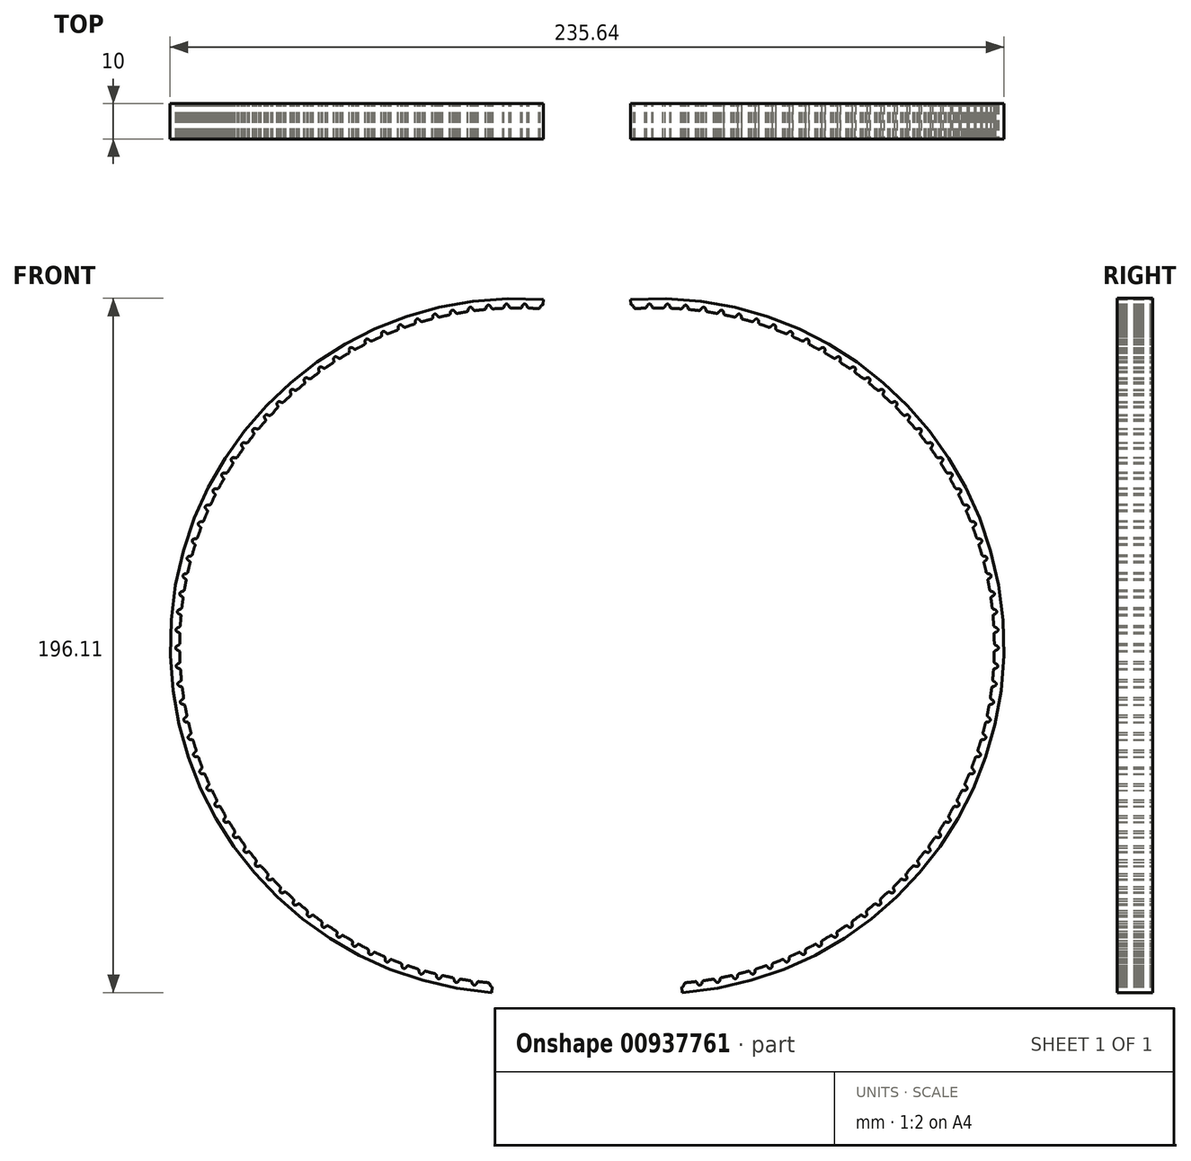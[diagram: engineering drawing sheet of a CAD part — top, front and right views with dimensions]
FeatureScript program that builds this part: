
annotation { "Feature Type Name" : "Feature", "Feature Type Description" : "" }
export const myFeature = defineFeature(function(context is Context, id is Id, definition is map)
    precondition{}
    {
        {
            var Q0;
            Q0=qCreatedBy(makeId("Front.planeOp"),FACE);
            var sketch = newSketch(context, id + "F0", { "sketchPlane" : qUnion([Q0])});
            skArc(sketch, "E0", {"start": v(26.92, -113.75) * mm, "mid": v(117.55, -8.54) * mm, "end": v(12.34, 82.09) * mm});
            skEllipticalArc(sketch, "E1.5.0.0", {});
            skArc(sketch, "E1.5.0.1", {"start": v(13.25, 79.82) * mm, "mid": v(13.37, 79.62) * mm, "end": v(13.55, 79.46) * mm});
            skEllipticalArc(sketch, "E1.5.0.3", {});
            skArc(sketch, "E2.1.0", {"start": v(16.42, 79.6) * mm, "mid": v(16.72, 79.76) * mm, "end": v(16.92, 80.04) * mm});
            skEllipticalArc(sketch, "E2.1.1", {});
            skArc(sketch, "E2.2.0", {"start": v(21.5, 79.64) * mm, "mid": v(21.81, 79.78) * mm, "end": v(22.03, 80.05) * mm});
            skEllipticalArc(sketch, "E2.2.1", {});
            skArc(sketch, "E2.3.0", {"start": v(26.58, 79.4) * mm, "mid": v(26.9, 79.53) * mm, "end": v(27.13, 79.79) * mm});
            skEllipticalArc(sketch, "E2.3.1", {});
            skArc(sketch, "E2.4.0", {"start": v(31.64, 78.9) * mm, "mid": v(31.96, 79) * mm, "end": v(32.2, 79.25) * mm});
            skEllipticalArc(sketch, "E2.4.1", {});
            skArc(sketch, "E2.5.0", {"start": v(36.67, 78.12) * mm, "mid": v(37, 78.22) * mm, "end": v(37.25, 78.45) * mm});
            skEllipticalArc(sketch, "E2.5.1", {});
            skArc(sketch, "E2.6.0", {"start": v(41.64, 77.08) * mm, "mid": v(41.98, 77.16) * mm, "end": v(42.24, 77.38) * mm});
            skEllipticalArc(sketch, "E2.6.1", {});
            skArc(sketch, "E2.7.0", {"start": v(46.56, 75.78) * mm, "mid": v(46.9, 75.84) * mm, "end": v(47.17, 76.04) * mm});
            skEllipticalArc(sketch, "E2.7.1", {});
            skArc(sketch, "E2.8.0", {"start": v(51.4, 74.22) * mm, "mid": v(51.73, 74.26) * mm, "end": v(52.02, 74.44) * mm});
            skEllipticalArc(sketch, "E2.8.1", {});
            skArc(sketch, "E2.9.0", {"start": v(56.14, 72.4) * mm, "mid": v(56.48, 72.42) * mm, "end": v(56.78, 72.6) * mm});
            skEllipticalArc(sketch, "E2.9.1", {});
            skArc(sketch, "E2.10.0", {"start": v(60.79, 70.33) * mm, "mid": v(61.13, 70.34) * mm, "end": v(61.43, 70.49) * mm});
            skEllipticalArc(sketch, "E2.10.1", {});
            skArc(sketch, "E2.11.0", {"start": v(65.31, 68.02) * mm, "mid": v(65.66, 68) * mm, "end": v(65.97, 68.14) * mm});
            skEllipticalArc(sketch, "E2.11.1", {});
            skArc(sketch, "E2.12.0", {"start": v(69.71, 65.47) * mm, "mid": v(70.05, 65.44) * mm, "end": v(70.37, 65.56) * mm});
            skEllipticalArc(sketch, "E2.12.1", {});
            skArc(sketch, "E2.13.0", {"start": v(73.97, 62.69) * mm, "mid": v(74.3, 62.64) * mm, "end": v(74.63, 62.74) * mm});
            skEllipticalArc(sketch, "E2.13.1", {});
            skArc(sketch, "E2.14.0", {"start": v(78.07, 59.69) * mm, "mid": v(78.4, 59.62) * mm, "end": v(78.74, 59.7) * mm});
            skEllipticalArc(sketch, "E2.14.1", {});
            skArc(sketch, "E2.15.0", {"start": v(82, 56.47) * mm, "mid": v(82.34, 56.38) * mm, "end": v(82.67, 56.45) * mm});
            skEllipticalArc(sketch, "E2.15.1", {});
            skArc(sketch, "E2.16.0", {"start": v(85.77, 53.05) * mm, "mid": v(86.1, 52.94) * mm, "end": v(86.43, 53) * mm});
            skEllipticalArc(sketch, "E2.16.1", {});
            skArc(sketch, "E2.17.0", {"start": v(89.34, 49.43) * mm, "mid": v(89.66, 49.3) * mm, "end": v(90, 49.34) * mm});
            skEllipticalArc(sketch, "E2.17.1", {});
            skArc(sketch, "E2.18.0", {"start": v(92.71, 45.63) * mm, "mid": v(93.03, 45.49) * mm, "end": v(93.37, 45.5) * mm});
            skEllipticalArc(sketch, "E2.18.1", {});
            skArc(sketch, "E2.19.0", {"start": v(95.88, 41.65) * mm, "mid": v(96.19, 41.5) * mm, "end": v(96.53, 41.5) * mm});
            skEllipticalArc(sketch, "E2.19.1", {});
            skArc(sketch, "E2.20.0", {"start": v(98.83, 37.5) * mm, "mid": v(99.13, 37.34) * mm, "end": v(99.47, 37.32) * mm});
            skEllipticalArc(sketch, "E2.20.1", {});
            skArc(sketch, "E2.21.0", {"start": v(101.56, 33.22) * mm, "mid": v(101.84, 33.03) * mm, "end": v(102.18, 33) * mm});
            skEllipticalArc(sketch, "E2.21.1", {});
            skArc(sketch, "E2.22.0", {"start": v(104.05, 28.79) * mm, "mid": v(104.33, 28.59) * mm, "end": v(104.67, 28.53) * mm});
            skEllipticalArc(sketch, "E2.22.1", {});
            skArc(sketch, "E2.23.0", {"start": v(106.3, 24.23) * mm, "mid": v(106.57, 24.02) * mm, "end": v(106.9, 23.94) * mm});
            skEllipticalArc(sketch, "E2.23.1", {});
            skArc(sketch, "E2.24.0", {"start": v(108.32, 19.56) * mm, "mid": v(108.57, 19.33) * mm, "end": v(108.9, 19.24) * mm});
            skEllipticalArc(sketch, "E2.24.1", {});
            skArc(sketch, "E2.25.0", {"start": v(110.08, 14.8) * mm, "mid": v(110.32, 14.55) * mm, "end": v(110.64, 14.44) * mm});
            skEllipticalArc(sketch, "E2.25.1", {});
            skArc(sketch, "E2.26.0", {"start": v(111.58, 9.93) * mm, "mid": v(111.8, 9.68) * mm, "end": v(112.12, 9.55) * mm});
            skEllipticalArc(sketch, "E2.26.1", {});
            skArc(sketch, "E2.27.0", {"start": v(112.82, 5) * mm, "mid": v(113.03, 4.74) * mm, "end": v(113.34, 4.6) * mm});
            skEllipticalArc(sketch, "E2.27.1", {});
            skArc(sketch, "E2.28.0", {"start": v(113.8, 0.02) * mm, "mid": v(114, -0.26) * mm, "end": v(114.3, -0.42) * mm});
            skEllipticalArc(sketch, "E2.28.1", {});
            skArc(sketch, "E2.29.0", {"start": v(114.5, -5.02) * mm, "mid": v(114.69, -5.3) * mm, "end": v(114.98, -5.48) * mm});
            skEllipticalArc(sketch, "E2.29.1", {});
            skArc(sketch, "E2.30.0", {"start": v(114.95, -10.08) * mm, "mid": v(115.12, -10.38) * mm, "end": v(115.4, -10.57) * mm});
            skEllipticalArc(sketch, "E2.30.1", {});
            skArc(sketch, "E2.31.0", {"start": v(115.12, -15.16) * mm, "mid": v(115.27, -15.47) * mm, "end": v(115.54, -15.68) * mm});
            skEllipticalArc(sketch, "E2.31.1", {});
            skArc(sketch, "E2.32.0", {"start": v(115.02, -20.25) * mm, "mid": v(115.15, -20.56) * mm, "end": v(115.41, -20.78) * mm});
            skEllipticalArc(sketch, "E2.32.1", {});
            skArc(sketch, "E2.33.0", {"start": v(114.65, -25.32) * mm, "mid": v(114.77, -25.64) * mm, "end": v(115.02, -25.87) * mm});
            skEllipticalArc(sketch, "E2.33.1", {});
            skArc(sketch, "E2.34.0", {"start": v(114, -30.36) * mm, "mid": v(114.1, -30.69) * mm, "end": v(114.35, -30.94) * mm});
            skEllipticalArc(sketch, "E2.34.1", {});
            skArc(sketch, "E2.35.0", {"start": v(113.1, -35.36) * mm, "mid": v(113.19, -35.7) * mm, "end": v(113.4, -35.96) * mm});
            skEllipticalArc(sketch, "E2.35.1", {});
            skArc(sketch, "E2.36.0", {"start": v(111.93, -40.31) * mm, "mid": v(112, -40.65) * mm, "end": v(112.2, -40.92) * mm});
            skEllipticalArc(sketch, "E2.36.1", {});
            skArc(sketch, "E2.37.0", {"start": v(110.5, -45.19) * mm, "mid": v(110.54, -45.53) * mm, "end": v(110.74, -45.8) * mm});
            skEllipticalArc(sketch, "E2.37.1", {});
            skArc(sketch, "E2.38.0", {"start": v(108.8, -49.98) * mm, "mid": v(108.83, -50.32) * mm, "end": v(109.01, -50.62) * mm});
            skEllipticalArc(sketch, "E2.38.1", {});
            skArc(sketch, "E2.39.0", {"start": v(106.86, -54.68) * mm, "mid": v(106.87, -55.02) * mm, "end": v(107.04, -55.32) * mm});
            skEllipticalArc(sketch, "E2.39.1", {});
            skArc(sketch, "E2.40.0", {"start": v(104.67, -59.27) * mm, "mid": v(104.66, -59.61) * mm, "end": v(104.8, -59.92) * mm});
            skEllipticalArc(sketch, "E2.40.1", {});
            skArc(sketch, "E2.41.0", {"start": v(102.24, -63.73) * mm, "mid": v(102.21, -64.07) * mm, "end": v(102.34, -64.4) * mm});
            skEllipticalArc(sketch, "E2.41.1", {});
            skArc(sketch, "E2.42.0", {"start": v(99.57, -68.06) * mm, "mid": v(99.53, -68.4) * mm, "end": v(99.64, -68.72) * mm});
            skEllipticalArc(sketch, "E2.42.1", {});
            skArc(sketch, "E2.43.0", {"start": v(96.68, -72.24) * mm, "mid": v(96.62, -72.58) * mm, "end": v(96.71, -72.9) * mm});
            skEllipticalArc(sketch, "E2.43.1", {});
            skArc(sketch, "E2.44.0", {"start": v(93.57, -76.26) * mm, "mid": v(93.49, -76.6) * mm, "end": v(93.57, -76.93) * mm});
            skEllipticalArc(sketch, "E2.44.1", {});
            skArc(sketch, "E2.45.0", {"start": v(90.25, -80.11) * mm, "mid": v(90.15, -80.44) * mm, "end": v(90.2, -80.78) * mm});
            skEllipticalArc(sketch, "E2.45.1", {});
            skArc(sketch, "E2.46.0", {"start": v(86.72, -83.78) * mm, "mid": v(86.61, -84.1) * mm, "end": v(86.65, -84.44) * mm});
            skEllipticalArc(sketch, "E2.46.1", {});
            skArc(sketch, "E2.47.0", {"start": v(83.01, -87.25) * mm, "mid": v(82.88, -87.57) * mm, "end": v(82.9, -87.91) * mm});
            skEllipticalArc(sketch, "E2.47.1", {});
            skArc(sketch, "E2.48.0", {"start": v(79.12, -90.53) * mm, "mid": v(78.98, -90.84) * mm, "end": v(78.98, -91.18) * mm});
            skEllipticalArc(sketch, "E2.48.1", {});
            skArc(sketch, "E2.49.0", {"start": v(75.06, -93.59) * mm, "mid": v(74.9, -93.89) * mm, "end": v(74.89, -94.23) * mm});
            skEllipticalArc(sketch, "E2.49.1", {});
            skArc(sketch, "E2.50.0", {"start": v(70.85, -96.43) * mm, "mid": v(70.67, -96.72) * mm, "end": v(70.64, -97.06) * mm});
            skEllipticalArc(sketch, "E2.50.1", {});
            skArc(sketch, "E2.51.0", {"start": v(66.48, -99.04) * mm, "mid": v(66.29, -99.32) * mm, "end": v(66.24, -99.66) * mm});
            skEllipticalArc(sketch, "E2.51.1", {});
            skArc(sketch, "E2.52.0", {"start": v(61.99, -101.41) * mm, "mid": v(61.78, -101.68) * mm, "end": v(61.71, -102.02) * mm});
            skEllipticalArc(sketch, "E2.52.1", {});
            skArc(sketch, "E2.53.0", {"start": v(57.37, -103.55) * mm, "mid": v(57.15, -103.8) * mm, "end": v(57.07, -104.14) * mm});
            skEllipticalArc(sketch, "E2.53.1", {});
            skArc(sketch, "E2.54.0", {"start": v(52.65, -105.43) * mm, "mid": v(52.42, -105.68) * mm, "end": v(52.31, -106) * mm});
            skEllipticalArc(sketch, "E2.54.1", {});
            skArc(sketch, "E2.55.0", {"start": v(47.84, -107.06) * mm, "mid": v(47.59, -107.3) * mm, "end": v(47.47, -107.62) * mm});
            skEllipticalArc(sketch, "E2.55.1", {});
            skArc(sketch, "E2.56.0", {"start": v(42.94, -108.43) * mm, "mid": v(42.68, -108.65) * mm, "end": v(42.54, -108.97) * mm});
            skEllipticalArc(sketch, "E2.56.1", {});
            skArc(sketch, "E2.57.0", {"start": v(37.98, -109.54) * mm, "mid": v(37.7, -109.75) * mm, "end": v(37.55, -110.06) * mm});
            skEllipticalArc(sketch, "E2.57.1", {});
            skArc(sketch, "E2.58.0", {"start": v(32.97, -110.39) * mm, "mid": v(32.68, -110.58) * mm, "end": v(32.51, -110.88) * mm});
            skEllipticalArc(sketch, "E2.58.1", {});
            skArc(sketch, "E2.59.0", {"start": v(27.92, -110.96) * mm, "mid": v(27.62, -111.14) * mm, "end": v(27.44, -111.43) * mm});
            skEllipticalArc(sketch, "E2.59.1", {});
            skLineSegment(sketch, "E2.anchor1", {"start": v(19.63, -15.83) * mm, "end": v(11.34, 79.3) * mm, "construction": true});
            skLineSegment(sketch, "E2.anchor2", {"start": v(19.63, -15.83) * mm, "end": v(27.92, -110.96) * mm, "construction": true});
            skArc(sketch, "E3.1.0", {"start": v(18.35, 80.02) * mm, "mid": v(18.46, 79.81) * mm, "end": v(18.63, 79.65) * mm});
            skArc(sketch, "E3.2.0", {"start": v(23.45, 79.96) * mm, "mid": v(23.55, 79.74) * mm, "end": v(23.7, 79.57) * mm});
            skArc(sketch, "E3.3.0", {"start": v(28.54, 79.62) * mm, "mid": v(28.63, 79.4) * mm, "end": v(28.78, 79.22) * mm});
            skArc(sketch, "E3.4.0", {"start": v(33.61, 79) * mm, "mid": v(33.69, 78.78) * mm, "end": v(33.83, 78.6) * mm});
            skArc(sketch, "E3.5.0", {"start": v(38.64, 78.13) * mm, "mid": v(38.7, 77.9) * mm, "end": v(38.83, 77.7) * mm});
            skArc(sketch, "E3.6.0", {"start": v(43.61, 76.98) * mm, "mid": v(43.66, 76.75) * mm, "end": v(43.78, 76.55) * mm});
            skArc(sketch, "E3.7.0", {"start": v(48.52, 75.58) * mm, "mid": v(48.56, 75.34) * mm, "end": v(48.67, 75.13) * mm});
            skArc(sketch, "E3.8.0", {"start": v(53.34, 73.9) * mm, "mid": v(53.37, 73.67) * mm, "end": v(53.47, 73.46) * mm});
            skArc(sketch, "E3.9.0", {"start": v(58.07, 71.99) * mm, "mid": v(58.08, 71.75) * mm, "end": v(58.17, 71.53) * mm});
            skArc(sketch, "E3.10.0", {"start": v(62.69, 69.82) * mm, "mid": v(62.7, 69.58) * mm, "end": v(62.77, 69.36) * mm});
            skArc(sketch, "E3.11.0", {"start": v(67.19, 67.4) * mm, "mid": v(67.18, 67.17) * mm, "end": v(67.24, 66.94) * mm});
            skArc(sketch, "E3.12.0", {"start": v(71.55, 64.75) * mm, "mid": v(71.53, 64.52) * mm, "end": v(71.58, 64.3) * mm});
            skArc(sketch, "E3.13.0", {"start": v(75.77, 61.88) * mm, "mid": v(75.73, 61.64) * mm, "end": v(75.77, 61.41) * mm});
            skArc(sketch, "E3.14.0", {"start": v(79.82, 58.78) * mm, "mid": v(79.77, 58.55) * mm, "end": v(79.8, 58.31) * mm});
            skArc(sketch, "E3.15.0", {"start": v(83.7, 55.47) * mm, "mid": v(83.65, 55.24) * mm, "end": v(83.66, 55) * mm});
            skArc(sketch, "E3.16.0", {"start": v(87.41, 51.96) * mm, "mid": v(87.34, 51.73) * mm, "end": v(87.34, 51.5) * mm});
            skArc(sketch, "E3.17.0", {"start": v(90.92, 48.25) * mm, "mid": v(90.83, 47.95) * mm, "end": v(90.86, 47.64) * mm});
            skArc(sketch, "E3.18.0", {"start": v(94.23, 44.37) * mm, "mid": v(94.12, 44.08) * mm, "end": v(94.14, 43.76) * mm});
            skArc(sketch, "E3.19.0", {"start": v(97.33, 40.31) * mm, "mid": v(97.2, 40.03) * mm, "end": v(97.2, 39.71) * mm});
            skArc(sketch, "E3.20.0", {"start": v(100.21, 36.1) * mm, "mid": v(100.07, 35.82) * mm, "end": v(100.05, 35.5) * mm});
            skArc(sketch, "E3.21.0", {"start": v(102.86, 31.74) * mm, "mid": v(102.7, 31.46) * mm, "end": v(102.67, 31.15) * mm});
            skArc(sketch, "E3.22.0", {"start": v(105.27, 27.24) * mm, "mid": v(105.1, 26.98) * mm, "end": v(105.05, 26.66) * mm});
            skArc(sketch, "E3.23.0", {"start": v(107.44, 22.62) * mm, "mid": v(107.26, 22.37) * mm, "end": v(107.2, 22.06) * mm});
            skArc(sketch, "E3.24.0", {"start": v(109.37, 17.9) * mm, "mid": v(109.17, 17.65) * mm, "end": v(109.09, 17.34) * mm});
            skArc(sketch, "E3.25.0", {"start": v(111.03, 13.07) * mm, "mid": v(110.82, 12.83) * mm, "end": v(110.73, 12.54) * mm});
            skArc(sketch, "E3.26.0", {"start": v(112.44, 8.16) * mm, "mid": v(112.22, 7.94) * mm, "end": v(112.1, 7.65) * mm});
            skArc(sketch, "E3.27.0", {"start": v(113.59, 3.19) * mm, "mid": v(113.35, 2.98) * mm, "end": v(113.23, 2.7) * mm});
            skArc(sketch, "E3.28.0", {"start": v(114.47, -1.84) * mm, "mid": v(114.22, -2.04) * mm, "end": v(114.08, -2.32) * mm});
            skArc(sketch, "E3.29.0", {"start": v(115.08, -6.9) * mm, "mid": v(114.82, -7.09) * mm, "end": v(114.66, -7.36) * mm});
            skArc(sketch, "E3.30.0", {"start": v(115.42, -12) * mm, "mid": v(115.15, -12.17) * mm, "end": v(114.98, -12.43) * mm});
            skArc(sketch, "E3.31.0", {"start": v(115.49, -17.1) * mm, "mid": v(115.21, -17.26) * mm, "end": v(115.03, -17.51) * mm});
            skArc(sketch, "E3.32.0", {"start": v(115.28, -22.2) * mm, "mid": v(115, -22.34) * mm, "end": v(114.8, -22.59) * mm});
            skArc(sketch, "E3.33.0", {"start": v(114.8, -27.28) * mm, "mid": v(114.52, -27.4) * mm, "end": v(114.3, -27.64) * mm});
            skArc(sketch, "E3.34.0", {"start": v(114.06, -32.33) * mm, "mid": v(113.77, -32.44) * mm, "end": v(113.54, -32.66) * mm});
            skArc(sketch, "E3.35.0", {"start": v(113.05, -37.34) * mm, "mid": v(112.75, -37.43) * mm, "end": v(112.52, -37.64) * mm});
            skArc(sketch, "E3.36.0", {"start": v(111.78, -42.28) * mm, "mid": v(111.47, -42.36) * mm, "end": v(111.22, -42.55) * mm});
            skArc(sketch, "E3.37.0", {"start": v(110.24, -47.14) * mm, "mid": v(109.93, -47.2) * mm, "end": v(109.67, -47.39) * mm});
            skArc(sketch, "E3.38.0", {"start": v(108.44, -51.92) * mm, "mid": v(108.13, -51.97) * mm, "end": v(107.86, -52.14) * mm});
            skArc(sketch, "E3.39.0", {"start": v(106.4, -56.6) * mm, "mid": v(106.08, -56.63) * mm, "end": v(105.8, -56.78) * mm});
            skArc(sketch, "E3.40.0", {"start": v(104.1, -61.16) * mm, "mid": v(103.79, -61.17) * mm, "end": v(103.5, -61.3) * mm});
            skArc(sketch, "E3.41.0", {"start": v(101.57, -65.59) * mm, "mid": v(101.26, -65.58) * mm, "end": v(100.97, -65.7) * mm});
            skArc(sketch, "E3.42.0", {"start": v(98.8, -69.88) * mm, "mid": v(98.5, -69.86) * mm, "end": v(98.2, -69.97) * mm});
            skArc(sketch, "E3.43.0", {"start": v(95.82, -74.02) * mm, "mid": v(95.5, -73.98) * mm, "end": v(95.2, -74.07) * mm});
            skArc(sketch, "E3.44.0", {"start": v(92.61, -77.99) * mm, "mid": v(92.3, -77.93) * mm, "end": v(92, -78.01) * mm});
            skArc(sketch, "E3.45.0", {"start": v(89.2, -81.79) * mm, "mid": v(88.9, -81.71) * mm, "end": v(88.59, -81.77) * mm});
            skArc(sketch, "E3.46.0", {"start": v(85.6, -85.4) * mm, "mid": v(85.3, -85.3) * mm, "end": v(84.98, -85.35) * mm});
            skArc(sketch, "E3.47.0", {"start": v(81.8, -88.8) * mm, "mid": v(81.5, -88.7) * mm, "end": v(81.19, -88.73) * mm});
            skArc(sketch, "E3.48.0", {"start": v(77.83, -92.01) * mm, "mid": v(77.53, -91.9) * mm, "end": v(77.22, -91.9) * mm});
            skArc(sketch, "E3.49.0", {"start": v(73.69, -95) * mm, "mid": v(73.4, -94.87) * mm, "end": v(73.09, -94.86) * mm});
            skArc(sketch, "E3.50.0", {"start": v(69.4, -97.77) * mm, "mid": v(69.12, -97.62) * mm, "end": v(68.8, -97.6) * mm});
            skArc(sketch, "E3.51.0", {"start": v(64.97, -100.3) * mm, "mid": v(64.7, -100.14) * mm, "end": v(64.39, -100.1) * mm});
            skArc(sketch, "E3.52.0", {"start": v(60.4, -102.6) * mm, "mid": v(60.15, -102.41) * mm, "end": v(59.84, -102.36) * mm});
            skArc(sketch, "E3.53.0", {"start": v(55.73, -104.64) * mm, "mid": v(55.48, -104.45) * mm, "end": v(55.18, -104.38) * mm});
            skArc(sketch, "E3.54.0", {"start": v(50.95, -106.44) * mm, "mid": v(50.72, -106.23) * mm, "end": v(50.41, -106.14) * mm});
            skArc(sketch, "E3.55.0", {"start": v(46.09, -107.97) * mm, "mid": v(45.86, -107.76) * mm, "end": v(45.56, -107.65) * mm});
            skArc(sketch, "E3.56.0", {"start": v(41.15, -109.25) * mm, "mid": v(40.93, -109.02) * mm, "end": v(40.64, -108.9) * mm});
            skArc(sketch, "E3.57.0", {"start": v(36.14, -110.27) * mm, "mid": v(35.94, -110.02) * mm, "end": v(35.66, -109.89) * mm});
            skArc(sketch, "E3.58.0", {"start": v(31.1, -111.01) * mm, "mid": v(30.9, -110.76) * mm, "end": v(30.63, -110.6) * mm});
            skLineSegment(sketch, "E3.anchor1", {"start": v(19.63, -15.83) * mm, "end": v(13.25, 79.82) * mm, "construction": true});
            skEllipticalArc(sketch, "E4.1.0", {});
            skEllipticalArc(sketch, "E4.2.0", {});
            skEllipticalArc(sketch, "E4.3.0", {});
            skEllipticalArc(sketch, "E4.4.0", {});
            skEllipticalArc(sketch, "E4.5.0", {});
            skEllipticalArc(sketch, "E4.6.0", {});
            skEllipticalArc(sketch, "E4.7.0", {});
            skEllipticalArc(sketch, "E4.8.0", {});
            skEllipticalArc(sketch, "E4.9.0", {});
            skEllipticalArc(sketch, "E4.10.0", {});
            skEllipticalArc(sketch, "E4.11.0", {});
            skEllipticalArc(sketch, "E4.12.0", {});
            skEllipticalArc(sketch, "E4.13.0", {});
            skEllipticalArc(sketch, "E4.14.0", {});
            skEllipticalArc(sketch, "E4.15.0", {});
            skEllipticalArc(sketch, "E4.16.0", {});
            skEllipticalArc(sketch, "E4.17.0", {});
            skEllipticalArc(sketch, "E4.18.0", {});
            skEllipticalArc(sketch, "E4.19.0", {});
            skEllipticalArc(sketch, "E4.20.0", {});
            skEllipticalArc(sketch, "E4.21.0", {});
            skEllipticalArc(sketch, "E4.22.0", {});
            skEllipticalArc(sketch, "E4.23.0", {});
            skEllipticalArc(sketch, "E4.24.0", {});
            skEllipticalArc(sketch, "E4.25.0", {});
            skEllipticalArc(sketch, "E4.26.0", {});
            skEllipticalArc(sketch, "E4.27.0", {});
            skEllipticalArc(sketch, "E4.28.0", {});
            skEllipticalArc(sketch, "E4.29.0", {});
            skEllipticalArc(sketch, "E4.30.0", {});
            skEllipticalArc(sketch, "E4.31.0", {});
            skEllipticalArc(sketch, "E4.32.0", {});
            skEllipticalArc(sketch, "E4.33.0", {});
            skEllipticalArc(sketch, "E4.34.0", {});
            skEllipticalArc(sketch, "E4.35.0", {});
            skEllipticalArc(sketch, "E4.36.0", {});
            skEllipticalArc(sketch, "E4.37.0", {});
            skEllipticalArc(sketch, "E4.38.0", {});
            skEllipticalArc(sketch, "E4.39.0", {});
            skEllipticalArc(sketch, "E4.40.0", {});
            skEllipticalArc(sketch, "E4.41.0", {});
            skEllipticalArc(sketch, "E4.42.0", {});
            skEllipticalArc(sketch, "E4.43.0", {});
            skEllipticalArc(sketch, "E4.44.0", {});
            skEllipticalArc(sketch, "E4.45.0", {});
            skEllipticalArc(sketch, "E4.46.0", {});
            skEllipticalArc(sketch, "E4.47.0", {});
            skEllipticalArc(sketch, "E4.48.0", {});
            skEllipticalArc(sketch, "E4.49.0", {});
            skEllipticalArc(sketch, "E4.50.0", {});
            skEllipticalArc(sketch, "E4.51.0", {});
            skEllipticalArc(sketch, "E4.52.0", {});
            skEllipticalArc(sketch, "E4.53.0", {});
            skEllipticalArc(sketch, "E4.54.0", {});
            skEllipticalArc(sketch, "E4.55.0", {});
            skEllipticalArc(sketch, "E4.56.0", {});
            skEllipticalArc(sketch, "E4.57.0", {});
            skEllipticalArc(sketch, "E4.58.0", {});
            skLineSegment(sketch, "E4.anchor1", {"start": v(19.63, -15.83) * mm, "end": v(12.53, 79.55) * mm, "construction": true});
            skLineSegment(sketch, "E4.anchor2", {"start": v(19.63, -15.83) * mm, "end": v(26.73, -111.21) * mm, "construction": true});
            skLineSegment(sketch, "E5", {"start": v(12.54, 79.4) * mm, "end": v(12.34, 82.09) * mm});
            skArc(sketch, "E6.trimOffspring", {"start": v(27.92, -110.96) * mm, "mid": v(29.35, -110.83) * mm, "end": v(30.78, -110.67) * mm});
            skLineSegment(sketch, "E7", {"start": v(26.77, -112.21) * mm, "end": v(26.92, -113.75) * mm});
            skArc(sketch, "E8.trimOffspring", {"start": v(32.97, -110.39) * mm, "mid": v(34.39, -110.18) * mm, "end": v(35.8, -109.94) * mm});
            skArc(sketch, "E9.trimOffspring", {"start": v(37.98, -109.54) * mm, "mid": v(39.39, -109.26) * mm, "end": v(40.8, -108.95) * mm});
            skArc(sketch, "E10.trimOffspring", {"start": v(42.94, -108.43) * mm, "mid": v(44.33, -108.07) * mm, "end": v(45.72, -107.69) * mm});
            skArc(sketch, "E11.trimOffspring", {"start": v(47.84, -107.06) * mm, "mid": v(49.2, -106.63) * mm, "end": v(50.57, -106.17) * mm});
            skArc(sketch, "E12.trimOffspring", {"start": v(52.65, -105.43) * mm, "mid": v(54, -104.92) * mm, "end": v(55.34, -104.4) * mm});
            skArc(sketch, "E13.trimOffspring", {"start": v(57.37, -103.55) * mm, "mid": v(58.7, -102.97) * mm, "end": v(60, -102.37) * mm});
            skArc(sketch, "E14.trimOffspring", {"start": v(61.99, -101.41) * mm, "mid": v(63.27, -100.77) * mm, "end": v(64.55, -100.1) * mm});
            skArc(sketch, "E15.trimOffspring", {"start": v(66.48, -99.04) * mm, "mid": v(67.73, -98.32) * mm, "end": v(68.97, -97.59) * mm});
            skArc(sketch, "E16.trimOffspring", {"start": v(70.85, -96.43) * mm, "mid": v(72.05, -95.65) * mm, "end": v(73.25, -94.85) * mm});
            skArc(sketch, "E17.trimOffspring", {"start": v(75.06, -93.59) * mm, "mid": v(76.23, -92.74) * mm, "end": v(77.38, -91.88) * mm});
            skArc(sketch, "E18.trimOffspring", {"start": v(79.12, -90.53) * mm, "mid": v(80.24, -89.62) * mm, "end": v(81.35, -88.7) * mm});
            skArc(sketch, "E19.trimOffspring", {"start": v(83.01, -87.25) * mm, "mid": v(84.08, -86.3) * mm, "end": v(85.14, -85.31) * mm});
            skArc(sketch, "E20.trimOffspring", {"start": v(86.72, -83.78) * mm, "mid": v(87.74, -82.76) * mm, "end": v(88.74, -81.73) * mm});
            skArc(sketch, "E21.trimOffspring", {"start": v(90.25, -80.11) * mm, "mid": v(91.2, -79.04) * mm, "end": v(92.15, -77.96) * mm});
            skArc(sketch, "E22.trimOffspring", {"start": v(93.57, -76.26) * mm, "mid": v(94.47, -75.14) * mm, "end": v(95.35, -74) * mm});
            skArc(sketch, "E23.trimOffspring", {"start": v(96.68, -72.24) * mm, "mid": v(97.52, -71.08) * mm, "end": v(98.34, -69.9) * mm});
            skArc(sketch, "E24.trimOffspring", {"start": v(99.57, -68.06) * mm, "mid": v(100.35, -66.85) * mm, "end": v(101.1, -65.63) * mm});
            skArc(sketch, "E25.trimOffspring", {"start": v(102.24, -63.73) * mm, "mid": v(102.95, -62.48) * mm, "end": v(103.64, -61.22) * mm});
            skArc(sketch, "E26.trimOffspring", {"start": v(104.67, -59.27) * mm, "mid": v(105.31, -57.98) * mm, "end": v(105.94, -56.69) * mm});
            skArc(sketch, "E27.trimOffspring", {"start": v(106.86, -54.68) * mm, "mid": v(107.44, -53.36) * mm, "end": v(108, -52.04) * mm});
            skArc(sketch, "E28.trimOffspring", {"start": v(108.8, -49.98) * mm, "mid": v(109.3, -48.64) * mm, "end": v(109.8, -47.28) * mm});
            skArc(sketch, "E29.trimOffspring", {"start": v(110.5, -45.19) * mm, "mid": v(110.93, -43.82) * mm, "end": v(111.34, -42.44) * mm});
            skArc(sketch, "E30.trimOffspring", {"start": v(111.93, -40.31) * mm, "mid": v(112.29, -38.92) * mm, "end": v(112.63, -37.52) * mm});
            skArc(sketch, "E31.trimOffspring", {"start": v(113.1, -35.36) * mm, "mid": v(113.39, -33.95) * mm, "end": v(113.65, -32.54) * mm});
            skArc(sketch, "E32.trimOffspring", {"start": v(114, -30.36) * mm, "mid": v(114.22, -28.94) * mm, "end": v(114.4, -27.51) * mm});
            skArc(sketch, "E33.trimOffspring", {"start": v(114.65, -25.32) * mm, "mid": v(114.78, -23.89) * mm, "end": v(114.9, -22.45) * mm});
            skArc(sketch, "E34.trimOffspring", {"start": v(115.02, -20.25) * mm, "mid": v(115.07, -18.81) * mm, "end": v(115.1, -17.37) * mm});
            skArc(sketch, "E35.trimOffspring", {"start": v(115.12, -15.16) * mm, "mid": v(115.1, -13.73) * mm, "end": v(115.05, -12.29) * mm});
            skArc(sketch, "E36.trimOffspring", {"start": v(114.95, -10.08) * mm, "mid": v(114.85, -8.65) * mm, "end": v(114.73, -7.21) * mm});
            skArc(sketch, "E37.trimOffspring", {"start": v(114.5, -5.02) * mm, "mid": v(114.33, -3.6) * mm, "end": v(114.14, -2.17) * mm});
            skArc(sketch, "E38.trimOffspring", {"start": v(113.8, 0.02) * mm, "mid": v(113.55, 1.43) * mm, "end": v(113.28, 2.85) * mm});
            skArc(sketch, "E39.trimOffspring", {"start": v(112.82, 5) * mm, "mid": v(112.5, 6.4) * mm, "end": v(112.15, 7.8) * mm});
            skArc(sketch, "E40.trimOffspring", {"start": v(111.58, 9.93) * mm, "mid": v(111.18, 11.32) * mm, "end": v(110.76, 12.7) * mm});
            skArc(sketch, "E41.trimOffspring", {"start": v(110.08, 14.8) * mm, "mid": v(109.6, 16.15) * mm, "end": v(109.11, 17.5) * mm});
            skArc(sketch, "E42.trimOffspring", {"start": v(108.32, 19.56) * mm, "mid": v(107.77, 20.9) * mm, "end": v(107.21, 22.22) * mm});
            skArc(sketch, "E43.trimOffspring", {"start": v(106.3, 24.23) * mm, "mid": v(105.7, 25.53) * mm, "end": v(105.06, 26.83) * mm});
            skArc(sketch, "E44.trimOffspring", {"start": v(104.05, 28.79) * mm, "mid": v(103.37, 30.06) * mm, "end": v(102.67, 31.31) * mm});
            skArc(sketch, "E45.trimOffspring", {"start": v(101.56, 33.22) * mm, "mid": v(100.81, 34.45) * mm, "end": v(100.04, 35.66) * mm});
            skArc(sketch, "E46.trimOffspring", {"start": v(98.83, 37.5) * mm, "mid": v(98.02, 38.7) * mm, "end": v(97.19, 39.87) * mm});
            skArc(sketch, "E47.trimOffspring", {"start": v(95.88, 41.65) * mm, "mid": v(95, 42.8) * mm, "end": v(94.11, 43.92) * mm});
            skArc(sketch, "E48.trimOffspring", {"start": v(92.71, 45.63) * mm, "mid": v(91.78, 46.72) * mm, "end": v(90.83, 47.8) * mm});
            skArc(sketch, "E49.trimOffspring", {"start": v(89.34, 49.43) * mm, "mid": v(88.35, 50.47) * mm, "end": v(87.34, 51.5) * mm});
            skArc(sketch, "E50.trimOffspring", {"start": v(85.77, 53.05) * mm, "mid": v(84.72, 54.03) * mm, "end": v(83.66, 55) * mm});
            skPoint(sketch, "E51.orphan", {"position": v(87.38, 51.34) * mm});
            skArc(sketch, "E52.trimOffspring", {"start": v(82, 56.47) * mm, "mid": v(80.91, 57.4) * mm, "end": v(79.8, 58.31) * mm});
            skPoint(sketch, "E53.orphan", {"position": v(83.71, 54.85) * mm});
            skArc(sketch, "E54.trimOffspring", {"start": v(78.07, 59.69) * mm, "mid": v(76.93, 60.56) * mm, "end": v(75.77, 61.41) * mm});
            skPoint(sketch, "E55.orphan", {"position": v(79.86, 58.16) * mm});
            skArc(sketch, "E56.trimOffspring", {"start": v(73.97, 62.69) * mm, "mid": v(72.78, 63.5) * mm, "end": v(71.58, 64.3) * mm});
            skPoint(sketch, "E57.orphan", {"position": v(75.84, 61.26) * mm});
            skArc(sketch, "E58.trimOffspring", {"start": v(69.71, 65.47) * mm, "mid": v(68.48, 66.21) * mm, "end": v(67.24, 66.94) * mm});
            skPoint(sketch, "E59.orphan", {"position": v(71.65, 64.15) * mm});
            skArc(sketch, "E60.trimOffspring", {"start": v(65.31, 68.02) * mm, "mid": v(64.05, 68.7) * mm, "end": v(62.77, 69.36) * mm});
            skPoint(sketch, "E61.orphan", {"position": v(67.32, 66.8) * mm});
            skArc(sketch, "E62.trimOffspring", {"start": v(60.79, 70.33) * mm, "mid": v(59.48, 70.94) * mm, "end": v(58.17, 71.53) * mm});
            skPoint(sketch, "E63.orphan", {"position": v(62.86, 69.22) * mm});
            skArc(sketch, "E64.trimOffspring", {"start": v(56.14, 72.4) * mm, "mid": v(54.8, 72.94) * mm, "end": v(53.47, 73.46) * mm});
            skPoint(sketch, "E65.orphan", {"position": v(58.27, 71.4) * mm});
            skArc(sketch, "E66.trimOffspring", {"start": v(51.4, 74.22) * mm, "mid": v(50.03, 74.69) * mm, "end": v(48.67, 75.13) * mm});
            skPoint(sketch, "E67.orphan", {"position": v(53.57, 73.34) * mm});
            skArc(sketch, "E68.trimOffspring", {"start": v(46.56, 75.78) * mm, "mid": v(45.17, 76.18) * mm, "end": v(43.78, 76.55) * mm});
            skPoint(sketch, "E69.orphan", {"position": v(48.78, 75.02) * mm});
            skArc(sketch, "E70.trimOffspring", {"start": v(41.64, 77.08) * mm, "mid": v(40.24, 77.4) * mm, "end": v(38.83, 77.7) * mm});
            skPoint(sketch, "E71.orphan", {"position": v(43.9, 76.44) * mm});
            skArc(sketch, "E72.trimOffspring", {"start": v(36.67, 78.12) * mm, "mid": v(35.25, 78.37) * mm, "end": v(33.83, 78.6) * mm});
            skPoint(sketch, "E73.orphan", {"position": v(38.95, 77.6) * mm});
            skArc(sketch, "E74.trimOffspring", {"start": v(31.64, 78.9) * mm, "mid": v(30.21, 79.07) * mm, "end": v(28.78, 79.22) * mm});
            skPoint(sketch, "E75.orphan", {"position": v(33.95, 78.5) * mm});
            skArc(sketch, "E76.trimOffspring", {"start": v(26.58, 79.4) * mm, "mid": v(25.15, 79.5) * mm, "end": v(23.7, 79.57) * mm});
            skPoint(sketch, "E77.orphan", {"position": v(28.91, 79.12) * mm});
            skArc(sketch, "E78.trimOffspring", {"start": v(21.5, 79.64) * mm, "mid": v(20.06, 79.66) * mm, "end": v(18.63, 79.65) * mm});
            skPoint(sketch, "E79.orphan", {"position": v(23.85, 79.48) * mm});
            skArc(sketch, "E80.trimOffspring", {"start": v(16.42, 79.6) * mm, "mid": v(14.98, 79.54) * mm, "end": v(13.55, 79.46) * mm});
            skPoint(sketch, "E81.orphan", {"position": v(18.77, 79.57) * mm});
            skPoint(sketch, "E82.orphan", {"position": v(13.7, 79.4) * mm});
            skPoint(sketch, "E83.orphan", {"position": v(11.82, 79.76) * mm});
            const initialGuessF0  = {"E1.5.0.0": [0.012530169083424244, 0.07954509625101978, -0.04082935197852619, 0.9991661343425395, 0.001, 0.0007199110732306023, 6.2831853071795845, 0.046258649843688854], "E1.5.0.3": [0.012530169083423734, 0.07954509625102026, -0.040829351978506234, 0.9991661343425403, 0.001, 0.00075, 4.9589597933309815, 0], "E2.1.1": [0.017616482165393188, 0.0797877933801241, 0.012406310336910385, 0.9999230387703968, 0.001, 0.0007199110732306023, 6.2831853071795845, 1.324225513848637], "E2.2.1": [0.0227085032628806, 0.0797594418893875, 0.06560680561779511, 0.9978455527067449, 0.001, 0.0007199110732306023, 6.2831853071795845, 1.324225513848637], "E2.3.1": [0.027791798488855504, 0.07946012214419074, 0.11862133128020791, 0.9929395650115425, 0.001, 0.0007199110732306023, 6.2831853071795845, 1.324225513848637], "E2.4.1": [0.03285195869071776, 0.07889068259887164, 0.17129961189131737, 0.9852189822399303, 0.001, 0.0007199110732306023, 6.2831853071795845, 1.324225513848637], "E2.5.1": [0.03787464029460662, 0.07805273739168897, 0.2234923251414217, 0.9747056892225884, 0.001, 0.0007199110732306023, 6.2831853071795845, 1.324225513848637], "E2.6.1": [0.04284560596381918, 0.07694866176937233, 0.275051525114259, 0.9614294870308068, 0.001, 0.0007199110732306023, 6.2831853071795845, 1.324225513848637], "E2.7.1": [0.047750764956088196, 0.07558158535422708, 0.32583106165578113, 0.9454280085021105, 0.001, 0.0007199110732306023, 6.2831853071795845, 1.324225513848637], "E2.8.1": [0.05257621306532181, 0.07395538327288, 0.37568699465264327, 0.9267466115658934, 0.001, 0.0007199110732306023, 6.2831853071795845, 1.324225513848637], "E2.9.1": [0.05730827203458649, 0.07207466517181176, 0.42447800204609437, 0.9054382506714392, 0.001, 0.0007199110732306023, 6.2831853071795845, 1.324225513848637], "E2.10.1": [0.061933528328612285, 0.06994476215081326, 0.4720657804247066, 0.8815633266827816, 0.001, 0.0007199110732306022, 6.2831853071795845, 1.324225513848637], "E2.11.1": [0.06643887115591601, 0.06757171165140397, 0.5183154370604216, 0.8551895156658926, 0.001, 0.0007199110732306023, 6.2831853071795845, 1.324225513848637], "E2.12.1": [0.07081152963276406, 0.06496224034304802, 0.5630958722766432, 0.8263915770535216, 0.001, 0.0007199110732306023, 6.2831853071795845, 1.324225513848637], "E2.13.1": [0.07503910898362987, 0.06212374505567886, 0.6062801510645143, 0.7952511417314595, 0.001, 0.0007199110732306023, 6.2831853071795845, 1.324225513848637], "E2.14.1": [0.07910962567553179, 0.059064271812581004, 0.647745862893991, 0.7618564806469255, 0.001, 0.0007199110732306023, 6.2831853071795845, 1.324225513848637], "E2.15.1": [0.08301154138665935, 0.05579249302306301, 0.6873754686997893, 0.7263022545949758, 0.001, 0.0007199110732306023, 6.2831853071795845, 1.324225513848637], "E2.16.1": [0.08673379571299994, 0.052317682899571005, 0.7250566340586357, 0.6886892458921962, 0.001, 0.0007199110732306023, 6.2831853071795845, 1.324225513848637], "E2.17.1": [0.09026583752025577, 0.048649691168925896, 0.7606825476133946, 0.6491240726982753, 0.001, 0.0007199110732306023, 6.2831853071795845, 1.324225513848637], "E2.18.1": [0.09359765485218027, 0.04479891515220258, 0.7941522238414651, 0.6077188867952482, 0.001, 0.0007199110732306023, 6.2831853071795845, 1.324225513848637], "E2.19.1": [0.09671980331055585, 0.0407762702923937, 0.8253707893092164, 0.5645910556810844, 0.001, 0.0007199110732306023, 6.2831853071795845, 1.324225513848637], "E2.20.1": [0.09962343282636688, 0.036593159213400575, 0.8542497516010429, 0.519862829878764, 0.001, 0.0007199110732306023, 6.2831853071795845, 1.324225513848637], "E2.21.1": [0.10230031274628161, 0.032261439398056896, 0.880707250160731, 0.47366099640388765, 0.001, 0.0007199110732306023, 6.2831853071795845, 1.324225513848637], "E2.22.1": [0.10474285516333351, 0.02779338957680533, 0.9046682883340994, 0.4261165193731064, 0.001, 0.0007199110732306023, 6.2831853071795845, 1.324225513848637], "E2.23.1": [0.10694413642566782, 0.0232016749223021, 0.9260649459551632, 0.3773641687721038, 0.001, 0.0007199110732306023, 6.2831853071795845, 1.324225513848637], "E2.24.1": [0.108897916762385, 0.018499311148609, 0.944836571873224, 0.3275421384354296, 0.001, 0.0007199110732306023, 6.2831853071795845, 1.324225513848637], "E2.25.1": [0.11059865797084927, 0.013699627616737806, 0.9609299558751463, 0.2767916543210608, 0.001, 0.0007199110732306023, 6.2831853071795845, 1.324225513848637], "E2.26.1": [0.1120415391153257, 0.00881622955112834, 0.9742994795154868, 0.2252565741900813, 0.001, 0.0007199110732306023, 6.2831853071795845, 1.324225513848637], "E2.27.1": [0.1132224701924463, 0.003862959474161565, 0.9849072454269355, 0.17308297982622728, 0.001, 0.0007199110732306023, 6.2831853071795845, 1.324225513848637], "E2.28.1": [0.11413810372476901, -0.0011461420319740711, 0.9927231847445203, 0.12041876295119949, 0.001, 0.0007199110732306023, 6.2831853071795845, 1.324225513848637], "E2.29.1": [0.11478584424956612, -0.0061968761248381455, 0.9977251423390708, 0.06741320600951253, 0.001, 0.0007199110732306023, 6.2831853071795845, 1.324225513848637], "E2.30.1": [0.1151638556759453, -0.011274925949899992, 0.9998989396183405, 0.014216559011184321, 0.001, 0.0007199110732306023, 6.2831853071795845, 1.324225513848637], "E2.31.1": [0.11527106648944889, -0.016365897223218254, 0.9992384147177656, -0.03902038636824013, 0.001, 0.0007199110732306023, 6.2831853071795845, 1.324225513848637], "E2.32.1": [0.11510717278937796, -0.021455359033602624, 0.9957454399669408, -0.09214672422307635, 0.001, 0.0007199110732306023, 6.2831853071795845, 1.324225513848637], "E2.33.1": [0.11467263915023183, -0.02652888474859949, 0.9894299165822965, -0.14501186217668555, 0.001, 0.0007199110732306023, 6.2831853071795845, 1.324225513848637], "E2.34.1": [0.1139686973048212, -0.031572092908348975, 0.9803097466010259, -0.19746594825192698, 0.001, 0.0007199110732306023, 6.2831853071795845, 1.324225513848637], "E2.35.1": [0.11299734265278771, -0.03657068799139547, 0.9684107821358152, -0.2493602956428686, 0.001, 0.0007199110732306023, 6.2831853071795845, 1.324225513848637], "E2.36.1": [0.11176132860442675, -0.041510500936896386, 0.9537667520942216, -0.3005478041836936, 0.001, 0.0007199110732306023, 6.2831853071795845, 1.324225513848637], "E2.37.1": [0.11026415877584703, -0.04637752930836438, 0.9364191665704203, -0.3508833773200998, 0.001, 0.0007199110732306023, 6.2831853071795845, 1.324225513848637], "E2.38.1": [0.10851007705758986, -0.051157976985095076, 0.9164171991803326, -0.4002243334012498, 0.001, 0.0007199110732306023, 6.2831853071795845, 1.324225513848637], "E2.39.1": [0.10650405558486045, -0.05583829326876996, 0.8938175476736688, -0.4484308101264104, 0.001, 0.0007199110732306022, 6.2831853071795845, 1.324225513848637], "E2.40.1": [0.1042517806434704, -0.06040521129438312, 0.8686842732179972, -0.4953661609998404, 0.001, 0.0007199110732306023, 6.2831853071795845, 1.324225513848637], "E2.41.1": [0.10175963655144282, -0.06484578563661138, 0.8410886188104042, -0.5408973426701287, 0.001, 0.0007199110732306023, 6.2831853071795845, 1.324225513848637], "E2.42.1": [0.09903468756196926, -0.06914742900502893, 0.8111088073314785, -0.5848952920560282, 0.001, 0.0007199110732306023, 6.2831853071795845, 1.324225513848637], "E2.43.1": [0.09608465783901643, -0.07329794792414963, 0.7788298198140581, -0.6272352921897826, 0.001, 0.0007199110732306023, 6.2831853071795845, 1.324225513848637], "E2.44.1": [0.09291790956234444, -0.07728557729715797, 0.7443431545552593, -0.6677973257409208, 0.001, 0.0007199110732306023, 6.2831853071795845, 1.324225513848637], "E2.45.1": [0.0895434192239995, -0.08109901375535424, 0.7077465677546129, -0.7064664152184201, 0.001, 0.0007199110732306022, 6.2831853071795845, 1.324225513848637], "E2.46.1": [0.08597075218347218, -0.0847274476987813, 0.6691437964134955, -0.7431329488868964, 0.001, 0.0007199110732306023, 6.2831853071795845, 1.324225513848637], "E2.47.1": [0.08221003555364648, -0.08816059393720994, 0.6286442642813282, -0.7776929914729769, 0.001, 0.0007199110732306023, 6.2831853071795845, 1.324225513848637], "E2.48.1": [0.07827192949439836, -0.09138872084462804, 0.5863627716820721, -0.8100485787811237, 0.001, 0.0007199110732306023, 6.2831853071795845, 1.324225513848637], "E2.49.1": [0.074167596995214, -0.09440267794459195, 0.542419170100234, -0.8401079953837921, 0.001, 0.0007199110732306023, 6.2831853071795845, 1.324225513848637], "E2.50.1": [0.06990867223248359, -0.09719392184824603, 0.49693802244881496, -0.867786034598772, 0.001, 0.0007199110732306023, 6.2831853071795845, 1.324225513848637], "E2.51.1": [0.06550722759116438, -0.09975454047148649, 0.4500482499822006, -0.8930042400167867, 0.001, 0.0007199110732306023, 6.2831853071795845, 1.324225513848637], "E2.52.1": [0.060975739444293485, -0.10207727546262363, 0.4018827668548544, -0.9156911278947104, 0.001, 0.0007199110732306023, 6.2831853071795845, 1.324225513848637], "E2.53.1": [0.05632705278735355, -0.10415554277696806, 0.3525781033617122, -0.9357823897840022, 0.001, 0.0007199110732306023, 6.2831853071795845, 1.324225513848637], "E2.54.1": [0.05157434482773708, -0.10598345134002088, 0.302274018928223, -0.9532210748199917, 0.001, 0.0007199110732306023, 6.2831853071795845, 1.324225513848637], "E2.55.1": [0.046731087632520485, -0.10755581974636427, 0.25111310594707403, -0.9679577511552938, 0.001, 0.0007199110732306023, 6.2831853071795845, 1.324225513848637], "E2.56.1": [0.041811009940426525, -0.10886819094691819, 0.19924038558456442, -0.9799506460797474, 0.001, 0.0007199110732306023, 6.2831853071795845, 1.324225513848637], "E2.57.1": [0.03682805824622256, -0.1099168448829301, 0.14680289670235003, -0.9891657644297033, 0.001, 0.0007199110732306023, 6.2831853071795845, 1.324225513848637], "E2.58.1": [0.03179635726786584, -0.11069880903088589, 0.09394927905981452, -0.9955769849510088, 0.001, 0.0007199110732306023, 6.2831853071795845, 1.324225513848637], "E2.59.1": [0.026730169908456197, -0.11121186682845051, 0.040829351978526315, -0.9991661343425395, 0.001, 0.0007199110732306023, 6.2831853071795845, 1.324225513848637], "E4.1.0": [0.017616482165392702, 0.0797877933801246, 0.012406310336930355, 0.9999230387703965, 0.001, 0.00075, 4.958959793330987, 0], "E4.2.0": [0.022708503262880143, 0.07975944188938801, 0.06560680561781504, 0.9978455527067436, 0.001, 0.00075, 4.958959793330987, 0], "E4.3.0": [0.027791798488855074, 0.07946012214419126, 0.11862133128022775, 0.9929395650115401, 0.001, 0.00075, 4.958959793330987, 0], "E4.4.0": [0.03285195869071736, 0.07889068259887219, 0.17129961189133702, 0.9852189822399269, 0.001, 0.00075, 4.958959793330987, 0], "E4.5.0": [0.03787464029460624, 0.07805273739168955, 0.22349232514144118, 0.9747056892225839, 0.001, 0.00075, 4.958959793330987, 0], "E4.6.0": [0.042845605963818846, 0.07694866176937296, 0.2750515251142782, 0.9614294870308012, 0.001, 0.00075, 4.958959793330987, 0], "E4.7.0": [0.04775076495608789, 0.07558158535422771, 0.3258310616558, 0.945428008502104, 0.001, 0.00075, 4.958959793330987, 0], "E4.8.0": [0.052576213065321536, 0.07395538327288063, 0.3756869946526617, 0.926746611565886, 0.001, 0.00075, 4.958959793330987, 0], "E4.9.0": [0.05730827203458625, 0.07207466517181241, 0.4244780020461124, 0.9054382506714307, 0.001, 0.00075, 4.958959793330987, 0], "E4.10.0": [0.06193352832861209, 0.06994476215081391, 0.47206578042472425, 0.8815633266827722, 0.001, 0.00075, 4.958959793330987, 0], "E4.11.0": [0.06643887115591585, 0.06757171165140463, 0.5183154370604387, 0.8551895156658823, 0.001, 0.00075, 4.958959793330987, 0], "E4.12.0": [0.07081152963276392, 0.06496224034304872, 0.5630958722766596, 0.8263915770535104, 0.001, 0.00075, 4.958959793330987, 0], "E4.13.0": [0.07503910898362978, 0.06212374505567955, 0.60628015106453, 0.7952511417314475, 0.001, 0.00075, 4.958959793330987, 0], "E4.14.0": [0.07910962567553173, 0.0590642718125817, 0.6477458628940063, 0.7618564806469125, 0.001, 0.00075, 4.958959793330987, 0], "E4.15.0": [0.08301154138665932, 0.0557924930230637, 0.6873754686998038, 0.726302254594962, 0.001, 0.00075, 4.958959793330987, 0], "E4.16.0": [0.08673379571299997, 0.0523176828995717, 0.7250566340586495, 0.6886892458921816, 0.001, 0.00075, 4.958959793330987, 0], "E4.17.0": [0.09026583752025585, 0.048649691168926576, 0.7606825476134076, 0.64912407269826, 0.001, 0.00075, 4.958959793330987, 0], "E4.18.0": [0.09359765485218036, 0.044798915152203266, 0.7941522238414772, 0.6077188867952323, 0.001, 0.00075, 4.958959793330987, 0], "E4.19.0": [0.09671980331055599, 0.04077627029239438, 0.8253707893092277, 0.5645910556810678, 0.001, 0.00075, 4.958959793330987, 0], "E4.20.0": [0.09962343282636704, 0.036593159213401255, 0.8542497516010532, 0.5198628298787469, 0.001, 0.00075, 4.958959793330987, 0], "E4.21.0": [0.10230031274628182, 0.03226143939805756, 0.8807072501607406, 0.47366099640387005, 0.001, 0.00075, 4.958959793330987, 0], "E4.22.0": [0.10474285516333376, 0.027793389576805987, 0.9046682883341078, 0.42611651937308836, 0.001, 0.00075, 4.958959793330987, 0], "E4.23.0": [0.1069441364256681, 0.02320167492230274, 0.9260649459551706, 0.3773641687720853, 0.001, 0.00075, 4.958959793330987, 0], "E4.24.0": [0.1088979167623853, 0.018499311148609622, 0.9448365718732306, 0.3275421384354107, 0.001, 0.00075, 4.958959793330987, 0], "E4.25.0": [0.11059865797084961, 0.013699627616738413, 0.9609299558751517, 0.2767916543210416, 0.001, 0.00075, 4.958959793330987, 0], "E4.26.0": [0.11204153911532606, 0.008816229551128929, 0.9742994795154913, 0.22525657419006187, 0.001, 0.00075, 4.958959793330987, 0], "E4.27.0": [0.1132224701924467, 0.0038629594741621323, 0.984907245426939, 0.17308297982620757, 0.001, 0.00075, 4.958959793330987, 0], "E4.28.0": [0.11413810372476946, -0.0011461420319735256, 0.9927231847445227, 0.12041876295117966, 0.001, 0.00075, 4.958959793330987, 0], "E4.29.0": [0.11478584424956657, -0.006196876124837623, 0.9977251423390722, 0.0674132060094926, 0.001, 0.00075, 4.958959793330987, 0], "E4.30.0": [0.11516385567594578, -0.011274925949899494, 0.9998989396183408, 0.01421655901116435, 0.001, 0.00075, 4.958959793330987, 0], "E4.31.0": [0.1152710664894494, -0.016365897223217785, 0.999238414717765, -0.039020386368260086, 0.001, 0.00075, 4.958959793330987, 0], "E4.32.0": [0.11510717278937851, -0.02145535903360218, 0.9957454399669389, -0.09214672422309622, 0.001, 0.00075, 4.958959793330987, 0], "E4.33.0": [0.11467263915023239, -0.026528884748599078, 0.9894299165822935, -0.1450118621767053, 0.001, 0.00075, 4.958959793330987, 0], "E4.34.0": [0.11396869730482179, -0.031572092908348594, 0.9803097466010219, -0.19746594825194652, 0.001, 0.00075, 4.958959793330987, 0], "E4.35.0": [0.11299734265278831, -0.03657068799139512, 0.9684107821358102, -0.24936029564288795, 0.001, 0.00075, 4.958959793330987, 0], "E4.36.0": [0.11176132860442736, -0.04151050093689606, 0.9537667520942157, -0.30054780418371263, 0.001, 0.00075, 4.958959793330987, 0], "E4.37.0": [0.11026415877584766, -0.04637752930836409, 0.9364191665704132, -0.3508833773201185, 0.001, 0.00075, 4.958959793330987, 0], "E4.38.0": [0.10851007705759051, -0.051157976985094826, 0.9164171991803246, -0.40022433340126806, 0.001, 0.00075, 4.958959793330987, 0], "E4.39.0": [0.10650405558486112, -0.05583829326876975, 0.8938175476736598, -0.44843081012642827, 0.001, 0.00075, 4.958959793330987, 0], "E4.40.0": [0.10425178064347108, -0.06040521129438294, 0.8686842732179875, -0.49536616099985775, 0.001, 0.00075, 4.958959793330987, 0], "E4.41.0": [0.10175963655144349, -0.06484578563661124, 0.8410886188103934, -0.5408973426701454, 0.001, 0.00075, 4.958959793330987, 0], "E4.42.0": [0.09903468756196993, -0.06914742900502882, 0.8111088073314668, -0.5848952920560444, 0.001, 0.00075, 4.958959793330987, 0], "E4.43.0": [0.09608465783901712, -0.07329794792414956, 0.7788298198140458, -0.6272352921897981, 0.001, 0.00075, 4.958959793330987, 0], "E4.44.0": [0.09291790956234514, -0.07728557729715793, 0.744343154555246, -0.6677973257409356, 0.001, 0.00075, 4.958959793330987, 0], "E4.45.0": [0.08954341922400019, -0.08109901375535424, 0.7077465677545988, -0.7064664152184342, 0.001, 0.00075, 4.958959793330987, 0], "E4.46.0": [0.08597075218347287, -0.08472744769878134, 0.6691437964134807, -0.7431329488869097, 0.001, 0.00075, 4.958959793330987, 0], "E4.47.0": [0.08221003555364717, -0.08816059393721001, 0.6286442642813127, -0.7776929914729894, 0.001, 0.00075, 4.958959793330987, 0], "E4.48.0": [0.07827192949439904, -0.09138872084462814, 0.5863627716820559, -0.8100485787811353, 0.001, 0.00075, 4.958959793330987, 0], "E4.49.0": [0.07416759699521466, -0.09440267794459209, 0.5424191701002172, -0.8401079953838029, 0.001, 0.00075, 4.958959793330987, 0], "E4.50.0": [0.06990867223248426, -0.09719392184824621, 0.4969380224487977, -0.8677860345987821, 0.001, 0.00075, 4.958959793330987, 0], "E4.51.0": [0.06550722759116503, -0.09975454047148671, 0.45004824998218274, -0.8930042400167957, 0.001, 0.00075, 4.958959793330987, 0], "E4.52.0": [0.06097573944429413, -0.1020772754626239, 0.4018827668548362, -0.9156911278947185, 0.001, 0.00075, 4.958959793330987, 0], "E4.53.0": [0.056327052787354184, -0.10415554277696837, 0.35257810336169343, -0.9357823897840091, 0.001, 0.00075, 4.958959793330987, 0], "E4.54.0": [0.051574344827737706, -0.1059834513400212, 0.30227401892820394, -0.9532210748199978, 0.001, 0.00075, 4.958959793330987, 0], "E4.55.0": [0.04673108763252108, -0.10755581974636463, 0.25111310594705466, -0.9679577511552988, 0.001, 0.00075, 4.958959793330987, 0], "E4.56.0": [0.04181100994042711, -0.10886819094691856, 0.19924038558454485, -0.9799506460797512, 0.001, 0.00075, 4.958959793330987, 0], "E4.57.0": [0.036828058246223115, -0.10991684488293052, 0.14680289670233027, -0.9891657644297062, 0.001, 0.00075, 4.958959793330987, 0], "E4.58.0": [0.03179635726786637, -0.11069880903088636, 0.09394927905979464, -0.9955769849510107, 0.001, 0.00075, 4.958959793330987, 0]};
            skSetInitialGuess(sketch, initialGuessF0);
            skSolve(sketch);
        }
        {
            var Q0;
            Q0=qSketchRegion(id+"F0",true);
            extrude(context, id + "F1", {"entities" : qUnion([Q0]), "depth" : 10 * mm, "offsetDistance" : 25 * mm});
        }
        {
            var Q0;
            Q0=makeQuery(id+"F1.opExtrude","SWEPT_BODY",BODY,{"disambiguationData":[OSD([sQuery(id+"F0.wireOp",EDGE,"E0"),sQuery(id+"F0.wireOp",EDGE,"E1.5.0.0"),sQuery(id+"F0.wireOp",EDGE,"E1.5.0.1"),sQuery(id+"F0.wireOp",EDGE,"E1.5.0.3"),sQuery(id+"F0.wireOp",EDGE,"E2.1.0"),sQuery(id+"F0.wireOp",EDGE,"E2.1.1"),sQuery(id+"F0.wireOp",EDGE,"E2.2.0"),sQuery(id+"F0.wireOp",EDGE,"E2.2.1"),sQuery(id+"F0.wireOp",EDGE,"E2.3.0"),sQuery(id+"F0.wireOp",EDGE,"E2.3.1"),sQuery(id+"F0.wireOp",EDGE,"E2.4.0"),sQuery(id+"F0.wireOp",EDGE,"E2.4.1"),sQuery(id+"F0.wireOp",EDGE,"E2.5.0"),sQuery(id+"F0.wireOp",EDGE,"E2.5.1"),sQuery(id+"F0.wireOp",EDGE,"E2.6.0"),sQuery(id+"F0.wireOp",EDGE,"E2.6.1"),sQuery(id+"F0.wireOp",EDGE,"E2.7.0"),sQuery(id+"F0.wireOp",EDGE,"E2.7.1"),sQuery(id+"F0.wireOp",EDGE,"E2.8.0"),sQuery(id+"F0.wireOp",EDGE,"E2.8.1"),sQuery(id+"F0.wireOp",EDGE,"E2.9.0"),sQuery(id+"F0.wireOp",EDGE,"E2.9.1"),sQuery(id+"F0.wireOp",EDGE,"E2.10.0"),sQuery(id+"F0.wireOp",EDGE,"E2.10.1"),sQuery(id+"F0.wireOp",EDGE,"E2.11.0"),sQuery(id+"F0.wireOp",EDGE,"E2.11.1"),sQuery(id+"F0.wireOp",EDGE,"E2.12.0"),sQuery(id+"F0.wireOp",EDGE,"E2.12.1"),sQuery(id+"F0.wireOp",EDGE,"E2.13.0"),sQuery(id+"F0.wireOp",EDGE,"E2.13.1"),sQuery(id+"F0.wireOp",EDGE,"E2.14.0"),sQuery(id+"F0.wireOp",EDGE,"E2.14.1"),sQuery(id+"F0.wireOp",EDGE,"E2.15.0"),sQuery(id+"F0.wireOp",EDGE,"E2.15.1"),sQuery(id+"F0.wireOp",EDGE,"E2.16.0"),sQuery(id+"F0.wireOp",EDGE,"E2.16.1"),sQuery(id+"F0.wireOp",EDGE,"E2.17.0"),sQuery(id+"F0.wireOp",EDGE,"E2.17.1"),sQuery(id+"F0.wireOp",EDGE,"E2.18.0"),sQuery(id+"F0.wireOp",EDGE,"E2.18.1"),sQuery(id+"F0.wireOp",EDGE,"E2.19.0"),sQuery(id+"F0.wireOp",EDGE,"E2.19.1"),sQuery(id+"F0.wireOp",EDGE,"E2.20.0"),sQuery(id+"F0.wireOp",EDGE,"E2.20.1"),sQuery(id+"F0.wireOp",EDGE,"E2.21.0"),sQuery(id+"F0.wireOp",EDGE,"E2.21.1"),sQuery(id+"F0.wireOp",EDGE,"E2.22.0"),sQuery(id+"F0.wireOp",EDGE,"E2.22.1"),sQuery(id+"F0.wireOp",EDGE,"E2.23.0"),sQuery(id+"F0.wireOp",EDGE,"E2.23.1"),sQuery(id+"F0.wireOp",EDGE,"E2.24.0"),sQuery(id+"F0.wireOp",EDGE,"E2.24.1"),sQuery(id+"F0.wireOp",EDGE,"E2.25.0"),sQuery(id+"F0.wireOp",EDGE,"E2.25.1"),sQuery(id+"F0.wireOp",EDGE,"E2.26.0"),sQuery(id+"F0.wireOp",EDGE,"E2.26.1"),sQuery(id+"F0.wireOp",EDGE,"E2.27.0"),sQuery(id+"F0.wireOp",EDGE,"E2.27.1"),sQuery(id+"F0.wireOp",EDGE,"E2.28.0"),sQuery(id+"F0.wireOp",EDGE,"E2.28.1"),sQuery(id+"F0.wireOp",EDGE,"E2.29.0"),sQuery(id+"F0.wireOp",EDGE,"E2.29.1"),sQuery(id+"F0.wireOp",EDGE,"E2.30.0"),sQuery(id+"F0.wireOp",EDGE,"E2.30.1"),sQuery(id+"F0.wireOp",EDGE,"E2.31.0"),sQuery(id+"F0.wireOp",EDGE,"E2.31.1"),sQuery(id+"F0.wireOp",EDGE,"E2.32.0"),sQuery(id+"F0.wireOp",EDGE,"E2.32.1"),sQuery(id+"F0.wireOp",EDGE,"E2.33.0"),sQuery(id+"F0.wireOp",EDGE,"E2.33.1"),sQuery(id+"F0.wireOp",EDGE,"E2.34.0"),sQuery(id+"F0.wireOp",EDGE,"E2.34.1"),sQuery(id+"F0.wireOp",EDGE,"E2.35.0"),sQuery(id+"F0.wireOp",EDGE,"E2.35.1"),sQuery(id+"F0.wireOp",EDGE,"E2.36.0"),sQuery(id+"F0.wireOp",EDGE,"E2.36.1"),sQuery(id+"F0.wireOp",EDGE,"E2.37.0"),sQuery(id+"F0.wireOp",EDGE,"E2.37.1"),sQuery(id+"F0.wireOp",EDGE,"E2.38.0"),sQuery(id+"F0.wireOp",EDGE,"E2.38.1"),sQuery(id+"F0.wireOp",EDGE,"E2.39.0"),sQuery(id+"F0.wireOp",EDGE,"E2.39.1"),sQuery(id+"F0.wireOp",EDGE,"E2.40.0"),sQuery(id+"F0.wireOp",EDGE,"E2.40.1"),sQuery(id+"F0.wireOp",EDGE,"E2.41.0"),sQuery(id+"F0.wireOp",EDGE,"E2.41.1"),sQuery(id+"F0.wireOp",EDGE,"E2.42.0"),sQuery(id+"F0.wireOp",EDGE,"E2.42.1"),sQuery(id+"F0.wireOp",EDGE,"E2.43.0"),sQuery(id+"F0.wireOp",EDGE,"E2.43.1"),sQuery(id+"F0.wireOp",EDGE,"E2.44.0"),sQuery(id+"F0.wireOp",EDGE,"E2.44.1"),sQuery(id+"F0.wireOp",EDGE,"E2.45.0"),sQuery(id+"F0.wireOp",EDGE,"E2.45.1"),sQuery(id+"F0.wireOp",EDGE,"E2.46.0"),sQuery(id+"F0.wireOp",EDGE,"E2.46.1"),sQuery(id+"F0.wireOp",EDGE,"E2.47.0"),sQuery(id+"F0.wireOp",EDGE,"E2.47.1"),sQuery(id+"F0.wireOp",EDGE,"E2.48.0"),sQuery(id+"F0.wireOp",EDGE,"E2.48.1"),sQuery(id+"F0.wireOp",EDGE,"E2.49.0"),sQuery(id+"F0.wireOp",EDGE,"E2.49.1"),sQuery(id+"F0.wireOp",EDGE,"E2.50.0"),sQuery(id+"F0.wireOp",EDGE,"E2.50.1"),sQuery(id+"F0.wireOp",EDGE,"E2.51.0"),sQuery(id+"F0.wireOp",EDGE,"E2.51.1"),sQuery(id+"F0.wireOp",EDGE,"E2.52.0"),sQuery(id+"F0.wireOp",EDGE,"E2.52.1"),sQuery(id+"F0.wireOp",EDGE,"E2.53.0"),sQuery(id+"F0.wireOp",EDGE,"E2.53.1"),sQuery(id+"F0.wireOp",EDGE,"E2.54.0"),sQuery(id+"F0.wireOp",EDGE,"E2.54.1"),sQuery(id+"F0.wireOp",EDGE,"E2.55.0"),sQuery(id+"F0.wireOp",EDGE,"E2.55.1"),sQuery(id+"F0.wireOp",EDGE,"E2.56.0"),sQuery(id+"F0.wireOp",EDGE,"E2.56.1"),sQuery(id+"F0.wireOp",EDGE,"E2.57.0"),sQuery(id+"F0.wireOp",EDGE,"E2.57.1"),sQuery(id+"F0.wireOp",EDGE,"E2.58.0"),sQuery(id+"F0.wireOp",EDGE,"E2.58.1"),sQuery(id+"F0.wireOp",EDGE,"E2.59.0"),sQuery(id+"F0.wireOp",EDGE,"E2.59.1"),sQuery(id+"F0.wireOp",EDGE,"E3.1.0"),sQuery(id+"F0.wireOp",EDGE,"E3.2.0"),sQuery(id+"F0.wireOp",EDGE,"E3.3.0"),sQuery(id+"F0.wireOp",EDGE,"E3.4.0"),sQuery(id+"F0.wireOp",EDGE,"E3.5.0"),sQuery(id+"F0.wireOp",EDGE,"E3.6.0"),sQuery(id+"F0.wireOp",EDGE,"E3.7.0"),sQuery(id+"F0.wireOp",EDGE,"E3.8.0"),sQuery(id+"F0.wireOp",EDGE,"E3.9.0"),sQuery(id+"F0.wireOp",EDGE,"E3.10.0"),sQuery(id+"F0.wireOp",EDGE,"E3.11.0"),sQuery(id+"F0.wireOp",EDGE,"E3.12.0"),sQuery(id+"F0.wireOp",EDGE,"E3.13.0"),sQuery(id+"F0.wireOp",EDGE,"E3.14.0"),sQuery(id+"F0.wireOp",EDGE,"E3.15.0"),sQuery(id+"F0.wireOp",EDGE,"E3.16.0"),sQuery(id+"F0.wireOp",EDGE,"E3.17.0"),sQuery(id+"F0.wireOp",EDGE,"E3.18.0"),sQuery(id+"F0.wireOp",EDGE,"E3.19.0"),sQuery(id+"F0.wireOp",EDGE,"E3.20.0"),sQuery(id+"F0.wireOp",EDGE,"E3.21.0"),sQuery(id+"F0.wireOp",EDGE,"E3.22.0"),sQuery(id+"F0.wireOp",EDGE,"E3.23.0"),sQuery(id+"F0.wireOp",EDGE,"E3.24.0"),sQuery(id+"F0.wireOp",EDGE,"E3.25.0"),sQuery(id+"F0.wireOp",EDGE,"E3.26.0"),sQuery(id+"F0.wireOp",EDGE,"E3.27.0"),sQuery(id+"F0.wireOp",EDGE,"E3.28.0"),sQuery(id+"F0.wireOp",EDGE,"E3.29.0"),sQuery(id+"F0.wireOp",EDGE,"E3.30.0"),sQuery(id+"F0.wireOp",EDGE,"E3.31.0"),sQuery(id+"F0.wireOp",EDGE,"E3.32.0"),sQuery(id+"F0.wireOp",EDGE,"E3.33.0"),sQuery(id+"F0.wireOp",EDGE,"E3.34.0"),sQuery(id+"F0.wireOp",EDGE,"E3.35.0"),sQuery(id+"F0.wireOp",EDGE,"E3.36.0"),sQuery(id+"F0.wireOp",EDGE,"E3.37.0"),sQuery(id+"F0.wireOp",EDGE,"E3.38.0"),sQuery(id+"F0.wireOp",EDGE,"E3.39.0"),sQuery(id+"F0.wireOp",EDGE,"E3.40.0"),sQuery(id+"F0.wireOp",EDGE,"E3.41.0"),sQuery(id+"F0.wireOp",EDGE,"E3.42.0"),sQuery(id+"F0.wireOp",EDGE,"E3.43.0"),sQuery(id+"F0.wireOp",EDGE,"E3.44.0"),sQuery(id+"F0.wireOp",EDGE,"E3.45.0"),sQuery(id+"F0.wireOp",EDGE,"E3.46.0"),sQuery(id+"F0.wireOp",EDGE,"E3.47.0"),sQuery(id+"F0.wireOp",EDGE,"E3.48.0"),sQuery(id+"F0.wireOp",EDGE,"E3.49.0"),sQuery(id+"F0.wireOp",EDGE,"E3.50.0"),sQuery(id+"F0.wireOp",EDGE,"E3.51.0"),sQuery(id+"F0.wireOp",EDGE,"E3.52.0"),sQuery(id+"F0.wireOp",EDGE,"E3.53.0"),sQuery(id+"F0.wireOp",EDGE,"E3.54.0"),sQuery(id+"F0.wireOp",EDGE,"E3.55.0"),sQuery(id+"F0.wireOp",EDGE,"E3.56.0"),sQuery(id+"F0.wireOp",EDGE,"E3.57.0"),sQuery(id+"F0.wireOp",EDGE,"E3.58.0"),sQuery(id+"F0.wireOp",EDGE,"E4.1.0"),sQuery(id+"F0.wireOp",EDGE,"E4.2.0"),sQuery(id+"F0.wireOp",EDGE,"E4.3.0"),sQuery(id+"F0.wireOp",EDGE,"E4.4.0"),sQuery(id+"F0.wireOp",EDGE,"E4.5.0"),sQuery(id+"F0.wireOp",EDGE,"E4.6.0"),sQuery(id+"F0.wireOp",EDGE,"E4.7.0"),sQuery(id+"F0.wireOp",EDGE,"E4.8.0"),sQuery(id+"F0.wireOp",EDGE,"E4.9.0"),sQuery(id+"F0.wireOp",EDGE,"E4.10.0"),sQuery(id+"F0.wireOp",EDGE,"E4.11.0"),sQuery(id+"F0.wireOp",EDGE,"E4.12.0"),sQuery(id+"F0.wireOp",EDGE,"E4.13.0"),sQuery(id+"F0.wireOp",EDGE,"E4.14.0"),sQuery(id+"F0.wireOp",EDGE,"E4.15.0"),sQuery(id+"F0.wireOp",EDGE,"E4.16.0"),sQuery(id+"F0.wireOp",EDGE,"E4.17.0"),sQuery(id+"F0.wireOp",EDGE,"E4.18.0"),sQuery(id+"F0.wireOp",EDGE,"E4.19.0"),sQuery(id+"F0.wireOp",EDGE,"E4.20.0"),sQuery(id+"F0.wireOp",EDGE,"E4.21.0"),sQuery(id+"F0.wireOp",EDGE,"E4.22.0"),sQuery(id+"F0.wireOp",EDGE,"E4.23.0"),sQuery(id+"F0.wireOp",EDGE,"E4.24.0"),sQuery(id+"F0.wireOp",EDGE,"E4.25.0"),sQuery(id+"F0.wireOp",EDGE,"E4.26.0"),sQuery(id+"F0.wireOp",EDGE,"E4.27.0"),sQuery(id+"F0.wireOp",EDGE,"E4.28.0"),sQuery(id+"F0.wireOp",EDGE,"E4.29.0"),sQuery(id+"F0.wireOp",EDGE,"E4.30.0"),sQuery(id+"F0.wireOp",EDGE,"E4.31.0"),sQuery(id+"F0.wireOp",EDGE,"E4.32.0"),sQuery(id+"F0.wireOp",EDGE,"E4.33.0"),sQuery(id+"F0.wireOp",EDGE,"E4.34.0"),sQuery(id+"F0.wireOp",EDGE,"E4.35.0"),sQuery(id+"F0.wireOp",EDGE,"E4.36.0"),sQuery(id+"F0.wireOp",EDGE,"E4.37.0"),sQuery(id+"F0.wireOp",EDGE,"E4.38.0"),sQuery(id+"F0.wireOp",EDGE,"E4.39.0"),sQuery(id+"F0.wireOp",EDGE,"E4.40.0"),sQuery(id+"F0.wireOp",EDGE,"E4.41.0"),sQuery(id+"F0.wireOp",EDGE,"E4.42.0"),sQuery(id+"F0.wireOp",EDGE,"E4.43.0"),sQuery(id+"F0.wireOp",EDGE,"E4.44.0"),sQuery(id+"F0.wireOp",EDGE,"E4.45.0"),sQuery(id+"F0.wireOp",EDGE,"E4.46.0"),sQuery(id+"F0.wireOp",EDGE,"E4.47.0"),sQuery(id+"F0.wireOp",EDGE,"E4.48.0"),sQuery(id+"F0.wireOp",EDGE,"E4.49.0"),sQuery(id+"F0.wireOp",EDGE,"E4.50.0"),sQuery(id+"F0.wireOp",EDGE,"E4.51.0"),sQuery(id+"F0.wireOp",EDGE,"E4.52.0"),sQuery(id+"F0.wireOp",EDGE,"E4.53.0"),sQuery(id+"F0.wireOp",EDGE,"E4.54.0"),sQuery(id+"F0.wireOp",EDGE,"E4.55.0"),sQuery(id+"F0.wireOp",EDGE,"E4.56.0"),sQuery(id+"F0.wireOp",EDGE,"E4.57.0"),sQuery(id+"F0.wireOp",EDGE,"E4.58.0"),sQuery(id+"F0.wireOp",EDGE,"E5"),sQuery(id+"F0.wireOp",EDGE,"E6.trimOffspring"),sQuery(id+"F0.wireOp",EDGE,"E7"),sQuery(id+"F0.wireOp",EDGE,"E8.trimOffspring"),sQuery(id+"F0.wireOp",EDGE,"E9.trimOffspring"),sQuery(id+"F0.wireOp",EDGE,"E10.trimOffspring"),sQuery(id+"F0.wireOp",EDGE,"E11.trimOffspring"),sQuery(id+"F0.wireOp",EDGE,"E12.trimOffspring"),sQuery(id+"F0.wireOp",EDGE,"E13.trimOffspring"),sQuery(id+"F0.wireOp",EDGE,"E14.trimOffspring"),sQuery(id+"F0.wireOp",EDGE,"E15.trimOffspring"),sQuery(id+"F0.wireOp",EDGE,"E16.trimOffspring"),sQuery(id+"F0.wireOp",EDGE,"E17.trimOffspring"),sQuery(id+"F0.wireOp",EDGE,"E18.trimOffspring"),sQuery(id+"F0.wireOp",EDGE,"E19.trimOffspring"),sQuery(id+"F0.wireOp",EDGE,"E20.trimOffspring"),sQuery(id+"F0.wireOp",EDGE,"E21.trimOffspring"),sQuery(id+"F0.wireOp",EDGE,"E22.trimOffspring"),sQuery(id+"F0.wireOp",EDGE,"E23.trimOffspring"),sQuery(id+"F0.wireOp",EDGE,"E24.trimOffspring"),sQuery(id+"F0.wireOp",EDGE,"E25.trimOffspring"),sQuery(id+"F0.wireOp",EDGE,"E26.trimOffspring"),sQuery(id+"F0.wireOp",EDGE,"E27.trimOffspring"),sQuery(id+"F0.wireOp",EDGE,"E28.trimOffspring"),sQuery(id+"F0.wireOp",EDGE,"E29.trimOffspring"),sQuery(id+"F0.wireOp",EDGE,"E30.trimOffspring"),sQuery(id+"F0.wireOp",EDGE,"E31.trimOffspring"),sQuery(id+"F0.wireOp",EDGE,"E32.trimOffspring"),sQuery(id+"F0.wireOp",EDGE,"E33.trimOffspring"),sQuery(id+"F0.wireOp",EDGE,"E34.trimOffspring"),sQuery(id+"F0.wireOp",EDGE,"E35.trimOffspring"),sQuery(id+"F0.wireOp",EDGE,"E36.trimOffspring"),sQuery(id+"F0.wireOp",EDGE,"E37.trimOffspring"),sQuery(id+"F0.wireOp",EDGE,"E38.trimOffspring"),sQuery(id+"F0.wireOp",EDGE,"E39.trimOffspring"),sQuery(id+"F0.wireOp",EDGE,"E40.trimOffspring"),sQuery(id+"F0.wireOp",EDGE,"E41.trimOffspring"),sQuery(id+"F0.wireOp",EDGE,"E42.trimOffspring"),sQuery(id+"F0.wireOp",EDGE,"E43.trimOffspring"),sQuery(id+"F0.wireOp",EDGE,"E44.trimOffspring"),sQuery(id+"F0.wireOp",EDGE,"E45.trimOffspring"),sQuery(id+"F0.wireOp",EDGE,"E46.trimOffspring"),sQuery(id+"F0.wireOp",EDGE,"E47.trimOffspring"),sQuery(id+"F0.wireOp",EDGE,"E48.trimOffspring"),sQuery(id+"F0.wireOp",EDGE,"E49.trimOffspring"),sQuery(id+"F0.wireOp",EDGE,"E50.trimOffspring"),sQuery(id+"F0.wireOp",EDGE,"E52.trimOffspring"),sQuery(id+"F0.wireOp",EDGE,"E54.trimOffspring"),sQuery(id+"F0.wireOp",EDGE,"E56.trimOffspring"),sQuery(id+"F0.wireOp",EDGE,"E58.trimOffspring"),sQuery(id+"F0.wireOp",EDGE,"E60.trimOffspring"),sQuery(id+"F0.wireOp",EDGE,"E62.trimOffspring"),sQuery(id+"F0.wireOp",EDGE,"E64.trimOffspring"),sQuery(id+"F0.wireOp",EDGE,"E66.trimOffspring"),sQuery(id+"F0.wireOp",EDGE,"E68.trimOffspring"),sQuery(id+"F0.wireOp",EDGE,"E70.trimOffspring"),sQuery(id+"F0.wireOp",EDGE,"E72.trimOffspring"),sQuery(id+"F0.wireOp",EDGE,"E74.trimOffspring"),sQuery(id+"F0.wireOp",EDGE,"E76.trimOffspring"),sQuery(id+"F0.wireOp",EDGE,"E78.trimOffspring"),sQuery(id+"F0.wireOp",EDGE,"E80.trimOffspring")])]});
            var Q1;
            Q1=qCreatedBy(makeId("Right.planeOp"),FACE);
            mirror(context, id + "F2", {"entities" : qUnion([Q0]), "mirrorPlane" : qUnion([Q1])});
        }
    });
